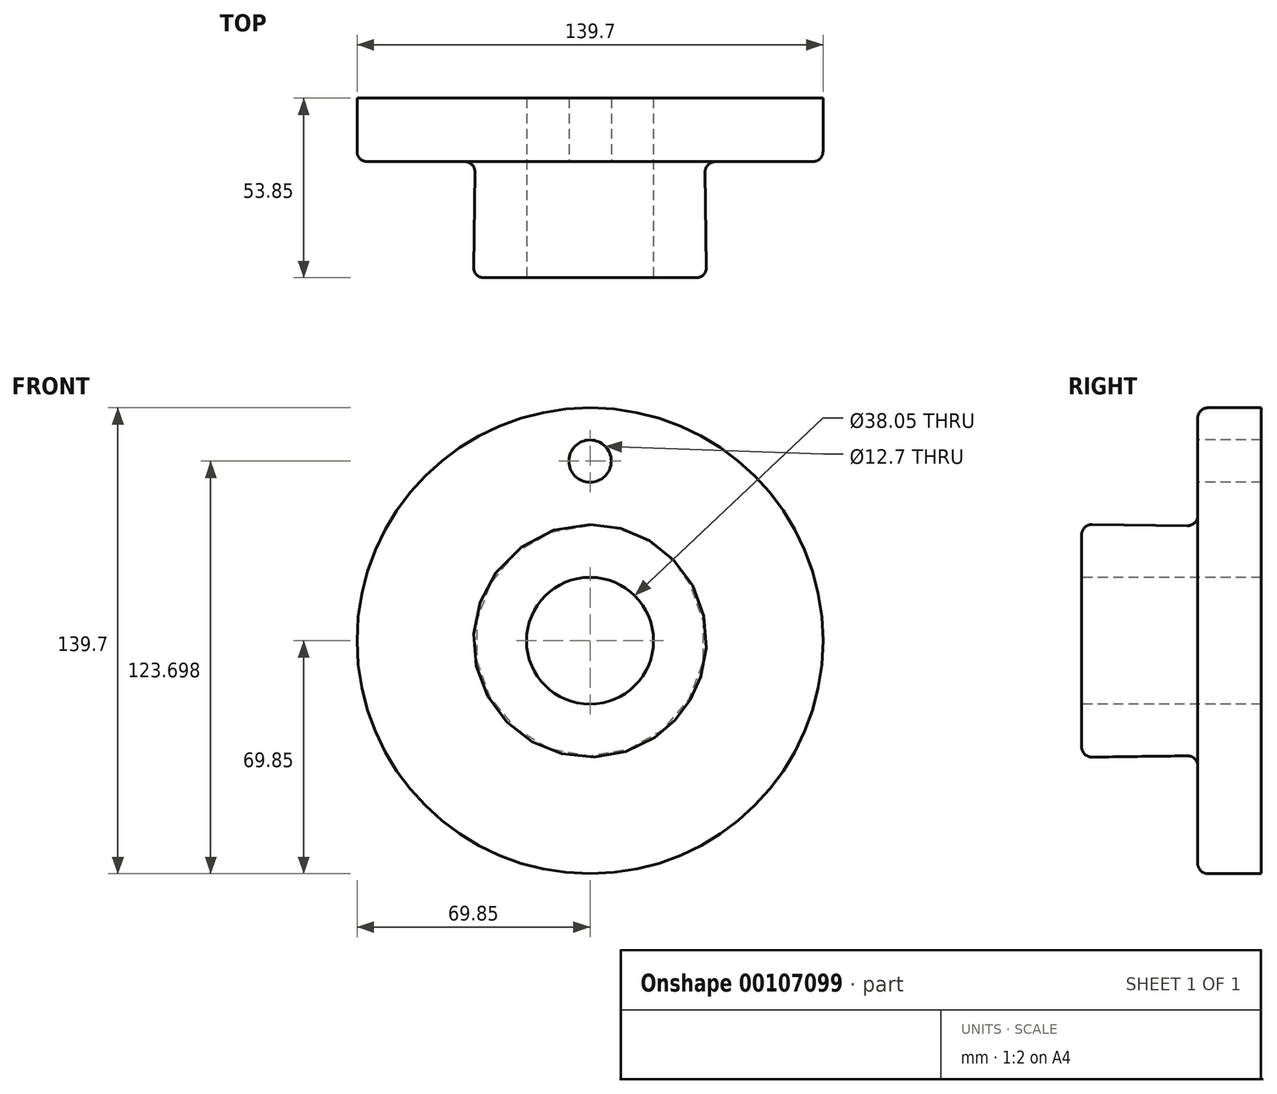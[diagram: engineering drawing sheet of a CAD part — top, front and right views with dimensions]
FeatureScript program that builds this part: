
annotation { "Feature Type Name" : "Feature", "Feature Type Description" : "" }
export const myFeature = defineFeature(function(context is Context, id is Id, definition is map)
    precondition{}
    {
        {
            var Q0;
            Q0=qCreatedBy(makeId("Right.planeOp"),FACE);
            var sketch = newSketch(context, id + "F0", { "sketchPlane" : qUnion([Q0])});
            skLineSegment(sketch, "E0", {"start": v(0, 34.93) * mm, "end": v(0, 0) * mm});
            skLineSegment(sketch, "E1", {"start": v(0, 0) * mm, "end": v(53.85, 0) * mm});
            skLineSegment(sketch, "E2", {"start": v(53.85, 0) * mm, "end": v(53.85, 69.85) * mm});
            skLineSegment(sketch, "E3", {"start": v(53.85, 69.85) * mm, "end": v(34.8, 69.85) * mm});
            skLineSegment(sketch, "E4", {"start": v(34.8, 69.85) * mm, "end": v(34.8, 34.46) * mm});
            skLineSegment(sketch, "E5", {"start": v(34.8, 34.46) * mm, "end": v(0, 34.93) * mm});
            skSolve(sketch);
        }
        {
            var Q0;
            Q0=makeQuery(id+"F0.imprint","IMPRINT",FACE,{"disambiguationData":[TD([[makeQuery(id+"F0.imprint","IMPRINT",EDGE,{"derivedFrom":sQuery(id+"F0.wireOp",EDGE,"E0")}),1.0]])]});
            var Q1;
            Q1=sQuery(id+"F0.wireOp",EDGE,"E1");
            revolve(context, id + "F1", {"entities" : qUnion([Q0]), "axis" : qUnion([Q1]), "revolveType" : RevolveType.FULL});
        }
        {
            var Q0;
            Q0=qCreatedBy(makeId("Front.planeOp"),FACE);
            var sketch = newSketch(context, id + "F2", { "sketchPlane" : qUnion([Q0])});
            skCircle(sketch, "E6", {"center": v(0, 0) * mm, "radius": 19.02 * mm});
            skSolve(sketch);
        }
        {
            var Q0;
            Q0 = qSketchRegion(id + "F2", true);
            extrude(context, id + "F3", {"entities" : qUnion([Q0]), "operationType" : NewBodyOperationType.REMOVE, "endBound" : BoundingType.THROUGH_ALL, "oppositeDirection" : true, "depth" : 25.4 * mm});
        }
        {
            var Q0;
            Q0=qCreatedBy(makeId("Front.planeOp"),FACE);
            var sketch = newSketch(context, id + "F4", { "sketchPlane" : qUnion([Q0])});
            skCircle(sketch, "E7", {"center": v(0, 53.85) * mm, "radius": 6.35 * mm});
            skSolve(sketch);
        }
        {
            var Q0;
            Q0 = qSketchRegion(id + "F4", true);
            extrude(context, id + "F5", {"entities" : qUnion([Q0]), "operationType" : NewBodyOperationType.REMOVE, "endBound" : BoundingType.THROUGH_ALL, "oppositeDirection" : true, "depth" : 25.4 * mm});
        }
        {
            var Q0;
            Q0=makeQuery(id+"F1.opRevolve","SWEPT_EDGE",EDGE,{"disambiguationData":[OSD([sQuery(id+"F0.wireOp",EDGE,"E0"),sQuery(id+"F0.wireOp",EDGE,"E5")])]});
            var Q1;
            Q1=makeQuery(id+"F3.boolean.opBoolean","COPY",EDGE,{"derivedFrom":makeQuery(id+"F3.opExtrude","CAP_EDGE",EDGE,{"disambiguationData":[OSD([sQuery(id+"F2.wireOp",EDGE,"E6")])],"isStart":true})});
            var Q2;
            Q2=makeQuery(id+"F1.opRevolve","SWEPT_EDGE",EDGE,{"disambiguationData":[OSD([sQuery(id+"F0.wireOp",EDGE,"E3"),sQuery(id+"F0.wireOp",EDGE,"E4")])]});
            var Q3;
            Q3=makeQuery(id+"F1.opRevolve","SWEPT_EDGE",EDGE,{"disambiguationData":[OSD([sQuery(id+"F0.wireOp",EDGE,"E4"),sQuery(id+"F0.wireOp",EDGE,"E5")])]});
            fillet(context, id + "F6", {"entities" : qUnion([Q0, Q1, Q2, Q3]), "radius" : 3.05 * mm, "tangentPropagation" : true, "allowEdgeOverflow" : false});
        }
    });
